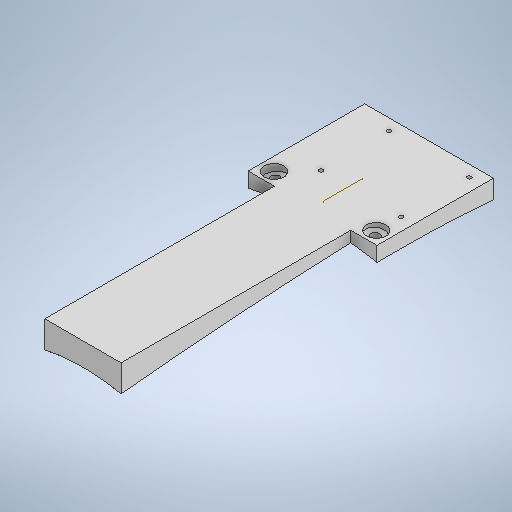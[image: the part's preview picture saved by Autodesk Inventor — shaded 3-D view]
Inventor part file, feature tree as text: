
AUTODESK INVENTOR PART (.ipt)
format: ipt  version: 2025 (Build 290162000, 162)  size: 519,168 bytes
history: native  units: in
note: dims shown in document units (in); Inventor stores cm internally (conversion verified against a paired STEP export)
features: sketch x13, extrude x10, other x4, mirror x2, loft x2, revolve x1, plane x1
ambient origin geometry x8: Origin, YZ Plane, XZ Plane, XY Plane, X Axis, Y Axis, Z Axis, Center Point
bodies: Solid1 (feature_tree)
feature tree (33):
  extrude  "Extrusion1"  Depth=1.5in
  revolve  "Revolution1"  [1 undecoded]
  extrude  "Extrusion2"  Depth=0.0563in
  plane  "Work Plane9"
  mirror  "Mirror1"
  extrude  "Extrusion3"  TaperAngle=90.0deg  [1 undecoded]
  mirror  "Mirror2"
  extrude  "Extrusion4"  TaperAngle=90.0deg  [1 undecoded]
  extrude  "Extrusion5"  Depth=0.6748in
  extrude  "Extrusion13"  TaperAngle=180.0deg  [1 undecoded]
  loft  "Loft4"
  extrude  "Extrusion14"  Depth=0.356in
  sketch  "Sketch21"  dims[d31=90.0deg d32=0.712in]
  extrude  "Extrusion16"  Depth=0.712in
  extrude  "Extrusion18"  Depth=2.585in
  loft  "Loft6"
  extrude  "Extrusion19"  Depth=0.11in
  sketch  "Sketch1"  dims[d2=0.25in d3=1.5in]
  sketch  "Sketch2"  dims[d4=1.0in d5=0.0in d6=0.1in]
  sketch  "Sketch3"  dims[d7=0.12in d8=0.0563in]
  sketch  "Sketch5"  dims[d9=0.2in d10=90.0deg]
  sketch  "Sketch6"  dims[d11=0.275in d12=90.0deg]
  sketch  "Sketch7"  dims[d13=0.15in d14=0.6748in]
  sketch  "Sketch8"  dims[d15=0.1in d16=180.0deg]
  sketch  "Sketch19"  dims[d17=1.0in d18=0.0in d27=-1.8228in]
  other  "Edges7"
  other  "Edges8"
  sketch  "Sketch20"  dims[d28=1.0in d29=0.0in d30=0.356in]
  sketch  "Sketch22"  dims[d33=1.0in d34=0.0in d52=2.585in]
  sketch  "Sketch25"  dims[d53=2.585in d54=0.36in]
  other  "Edges11"
  other  "Edges12"
  sketch  "Sketch26"  dims[d55=0.33in d56=0.11in d57=2.27in d58=1.93in d59=0.11in d60=0.11in d61=0.11in d62=0.2in d63=0.0in d64=0.345in d65=0.099in d66=0.099in d76=0.11in d113=0.01in d114=0.01in d115=0.01in d116=0.001in d117=0.0in d118=29.638in d119=0.0in d120=90.0deg d121=0.0in d122=90.0deg d123=0.0in d124=90.0deg d125=6.5in d126=1.08in d127=1.08in d128=0.1in d129=0.0in d130=0.51in d131=0.08in d132=0.08in d133=0.075in d134=0.075in d135=0.075in d136=90.0deg d139=0.001in d140=0.0in d156=0.036in d157=0.036in d158=0.06in d159=0.06in d160=0.06in d161=0.001in d162=0.0in d163=100.0in d164=0.0in d165=90.0deg d166=0.0in d167=90.0deg d168=0.0in d169=90.0deg d170=0.113in d171=0.113in d172=0.113in d173=0.113in d174=10.0in d175=0.0in d95=0.5in d96=0.0344in d97=0.5in d98=0.0344in]
note: 4 required parameter values undecoded (feature->parameter linkage not recoverable at this tier; creation-order binding heuristic only, values carry confidence <= 0.55)